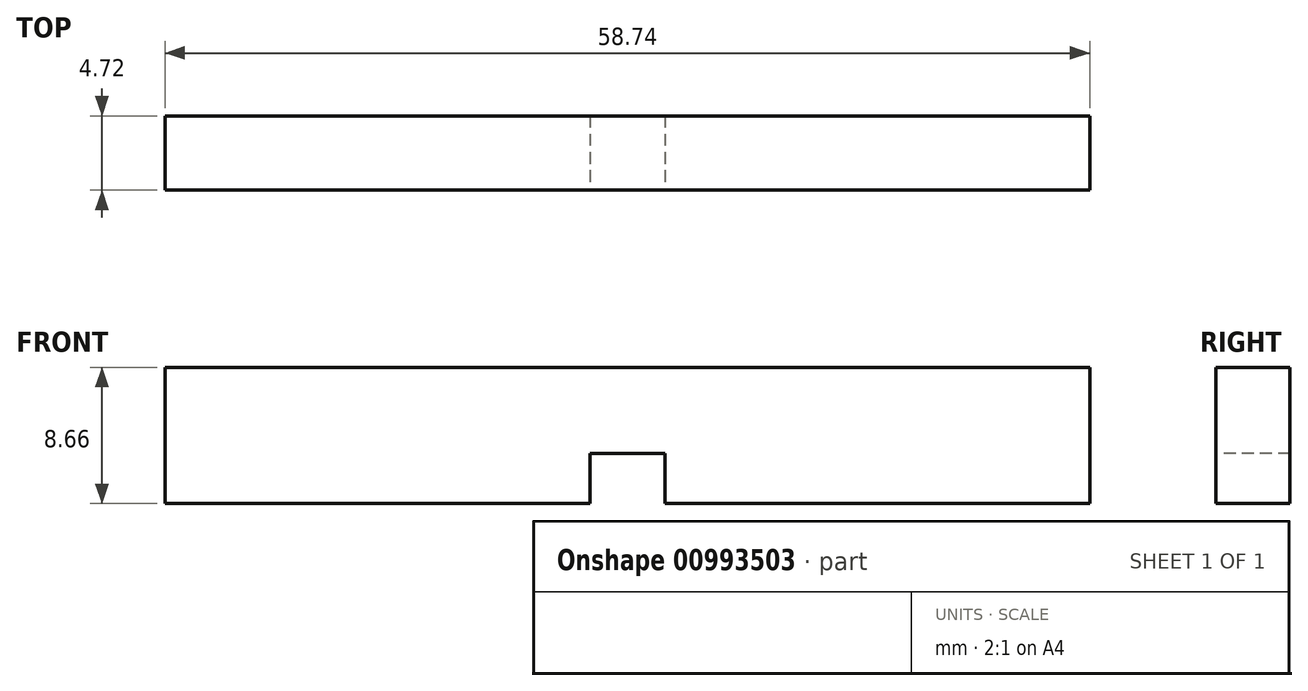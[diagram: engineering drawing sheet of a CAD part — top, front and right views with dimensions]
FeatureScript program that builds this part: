
annotation { "Feature Type Name" : "Feature", "Feature Type Description" : "" }
export const myFeature = defineFeature(function(context is Context, id is Id, definition is map)
    precondition{}
    {
        {
            var Q0;
            Q0=qCreatedBy(makeId("Front.planeOp"),FACE);
            var sketch = newSketch(context, id + "F0", { "sketchPlane" : qUnion([Q0])});
            skLineSegment(sketch, "E0.bottom", {"start": v(29.37, -4.33) * mm, "end": v(-29.37, -4.33) * mm});
            skLineSegment(sketch, "E0.top", {"start": v(29.37, 4.33) * mm, "end": v(-29.37, 4.33) * mm});
            skLineSegment(sketch, "E0.left", {"start": v(29.37, -4.33) * mm, "end": v(29.37, 4.33) * mm});
            skLineSegment(sketch, "E0.right", {"start": v(-29.37, -4.33) * mm, "end": v(-29.37, 4.33) * mm});
            skPoint(sketch, "E0.middle", {"position": v(0, 0) * mm});
            skSolve(sketch);
        }
        {
            var Q0;
            Q0=makeQuery(id+"F0.imprint","IMPRINT",FACE,{"disambiguationData":[TD([[makeQuery(id+"F0.imprint","IMPRINT",EDGE,{"derivedFrom":sQuery(id+"F0.wireOp",EDGE,"E0.bottom")}),-1.0]])]});
            extrude(context, id + "F1", {"entities" : qUnion([Q0]), "depth" : 4.72 * mm, "offsetDistance" : 25.4 * mm});
        }
        {
            var Q0;
            Q0=makeQuery(id+"F1.opExtrude","CAP_FACE",FACE,{"disambiguationData":[OSD([sQuery(id+"F0.wireOp",EDGE,"E0.bottom"),sQuery(id+"F0.wireOp",EDGE,"E0.top"),sQuery(id+"F0.wireOp",EDGE,"E0.left"),sQuery(id+"F0.wireOp",EDGE,"E0.right")])],"isStart":false});
            var sketch = newSketch(context, id + "F2", { "sketchPlane" : qUnion([Q0])});
            skLineSegment(sketch, "E1", {"start": v(0, -4.33) * mm, "end": v(-2.38, -4.33) * mm});
            skLineSegment(sketch, "E2", {"start": v(-2.38, -4.33) * mm, "end": v(2.38, -4.33) * mm});
            skLineSegment(sketch, "E3", {"start": v(2.38, -4.33) * mm, "end": v(2.38, -1.16) * mm});
            skLineSegment(sketch, "E4", {"start": v(-2.38, -4.33) * mm, "end": v(-2.38, -1.16) * mm});
            skLineSegment(sketch, "E5", {"start": v(-2.38, -1.16) * mm, "end": v(2.38, -1.16) * mm});
            skSolve(sketch);
        }
        {
            var Q0;
            {var subQ0=sQuery(id+"F2.wireOp",EDGE,"E3");Q0=makeQuery(id+"F2.imprint","IMPRINT",FACE,{"disambiguationData":[TD([[makeQuery(id+"F2.imprint","IMPRINT",EDGE,{"derivedFrom":subQ0}),1.0]])]});}
            extrude(context, id + "F3", {"entities" : qUnion([Q0]), "operationType" : NewBodyOperationType.REMOVE, "oppositeDirection" : true, "depth" : 25.4 * mm, "offsetDistance" : 25.4 * mm});
        }
    });
